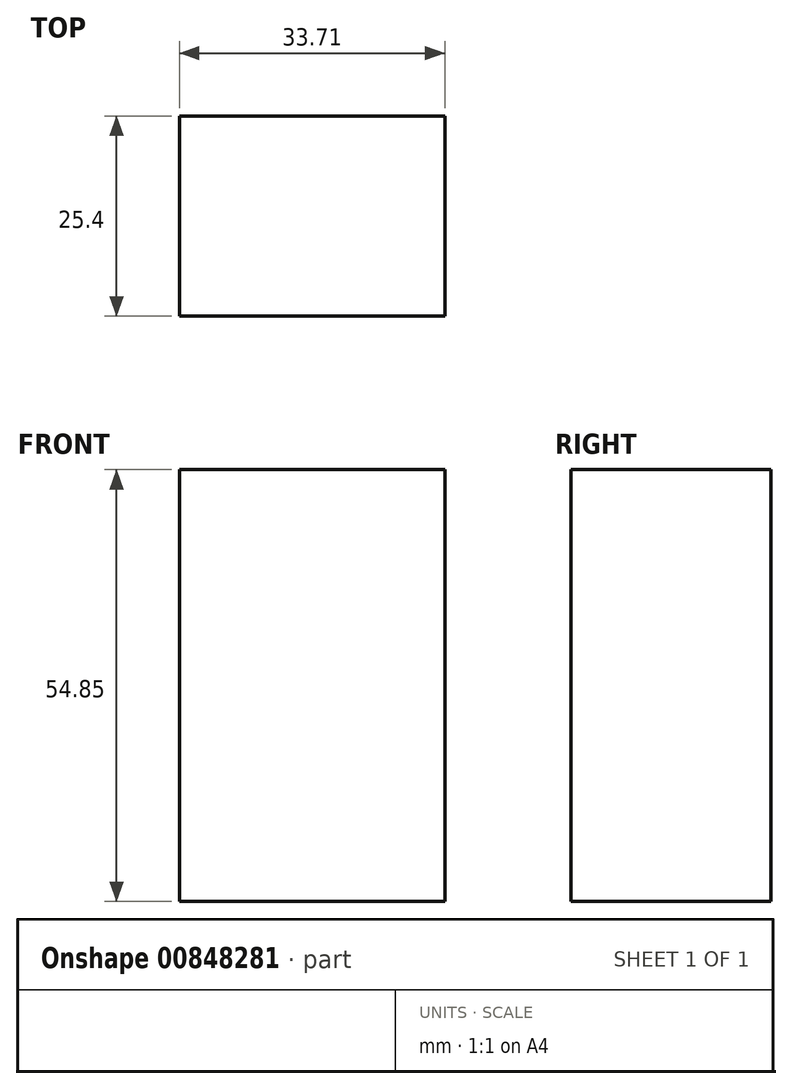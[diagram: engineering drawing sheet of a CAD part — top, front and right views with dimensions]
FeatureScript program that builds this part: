
annotation { "Feature Type Name" : "Feature", "Feature Type Description" : "" }
export const myFeature = defineFeature(function(context is Context, id is Id, definition is map)
    precondition{}
    {
        {
            var Q0;
            Q0=qCreatedBy(makeId("Front.planeOp"),FACE);
            var sketch = newSketch(context, id + "F0", { "sketchPlane" : qUnion([Q0])});
            skLineSegment(sketch, "E0.bottom", {"start": v(0, 0) * mm, "end": v(33.71, 0) * mm});
            skLineSegment(sketch, "E0.top", {"start": v(0, -54.85) * mm, "end": v(33.71, -54.85) * mm});
            skLineSegment(sketch, "E0.left", {"start": v(0, 0) * mm, "end": v(0, -54.85) * mm});
            skLineSegment(sketch, "E0.right", {"start": v(33.71, 0) * mm, "end": v(33.71, -54.85) * mm});
            skSolve(sketch);
        }
        {
            var Q0;
            Q0=makeQuery(id+"F0.imprint","IMPRINT",FACE,{"disambiguationData":[TD([[makeQuery(id+"F0.imprint","IMPRINT",EDGE,{"derivedFrom":sQuery(id+"F0.wireOp",EDGE,"E0.bottom")}),-1.0]])]});
            extrude(context, id + "F1", {"entities" : qUnion([Q0]), "depth" : 25.4 * mm, "offsetDistance" : 25.4 * mm});
        }
    });
